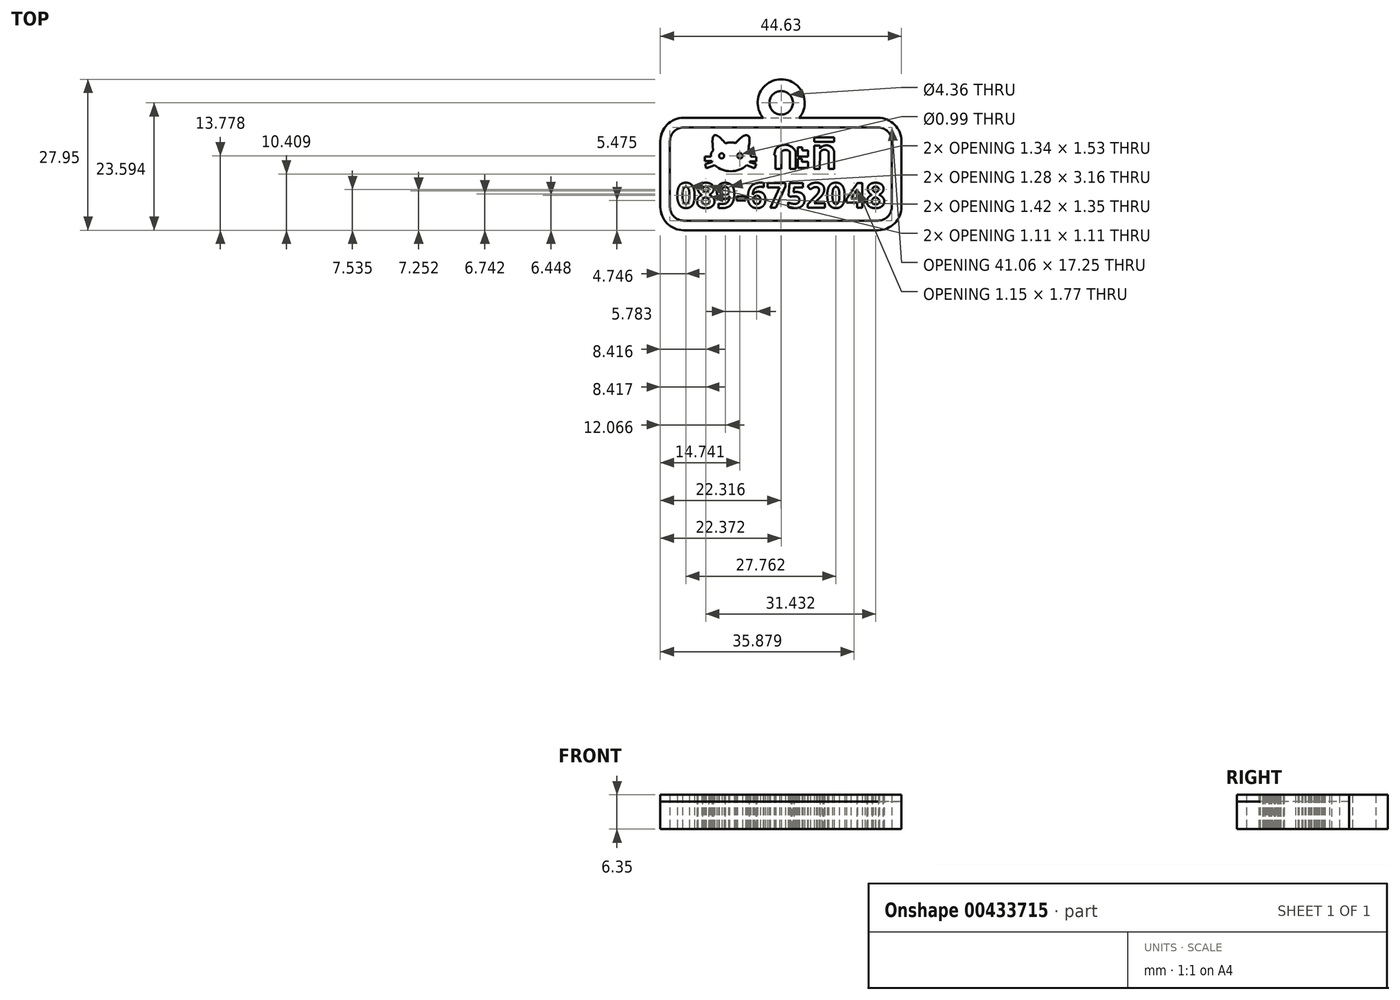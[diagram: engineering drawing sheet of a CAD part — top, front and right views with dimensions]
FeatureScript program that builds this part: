
annotation { "Feature Type Name" : "Feature", "Feature Type Description" : "" }
export const myFeature = defineFeature(function(context is Context, id is Id, definition is map)
    precondition{}
    {
        {
            var Q0;
            Q0=qCreatedBy(makeId("Top.planeOp"),FACE);
            var sketch = newSketch(context, id + "F0", { "sketchPlane" : qUnion([Q0])});
            skPoint(sketch, "E0.middle", {"position": v(0, 0) * mm});
            skLineSegment(sketch, "E1", {"start": v(-2.05, 4.59) * mm, "end": v(-3.13, 4.59) * mm});
            skLineSegment(sketch, "E2", {"start": v(-3.13, 4.59) * mm, "end": v(-3.13, 7.1) * mm});
            skLineSegment(sketch, "E3", {"start": v(-3.13, 7.1) * mm, "end": v(-3.43, 7.1) * mm});
            skLineSegment(sketch, "E4", {"start": v(-3.43, 7.1) * mm, "end": v(-3.16, 8.15) * mm});
            skLineSegment(sketch, "E5", {"start": v(-2.05, 6.13) * mm, "end": v(-2.05, 7.74) * mm});
            skLineSegment(sketch, "E6", {"start": v(-0.46, 7.74) * mm, "end": v(-0.46, 4.59) * mm});
            skLineSegment(sketch, "E7", {"start": v(-0.46, 4.59) * mm, "end": v(0.6, 4.59) * mm});
            skLineSegment(sketch, "E8", {"start": v(0.6, 4.59) * mm, "end": v(0.6, 7.74) * mm});
            skArc(sketch, "E9", {"start": v(-0.46, 7.74) * mm, "mid": v(-1.25, 8.09) * mm, "end": v(-2.05, 7.74) * mm});
            skArc(sketch, "E10", {"start": v(0.6, 7.74) * mm, "mid": v(-1.16, 9.03) * mm, "end": v(-3.16, 8.15) * mm});
            skLineSegment(sketch, "E11", {"start": v(4, 8.88) * mm, "end": v(4, 4.6) * mm});
            skLineSegment(sketch, "E12", {"start": v(4, 4.6) * mm, "end": v(5.01, 4.57) * mm});
            skLineSegment(sketch, "E13", {"start": v(5.01, 4.57) * mm, "end": v(5.08, 7.6) * mm});
            skLineSegment(sketch, "E14", {"start": v(4, 8.88) * mm, "end": v(5.08, 8.88) * mm});
            skLineSegment(sketch, "E15", {"start": v(5.08, 8.88) * mm, "end": v(5.08, 8.34) * mm});
            skLineSegment(sketch, "E16", {"start": v(6.67, 7.73) * mm, "end": v(6.67, 4.57) * mm});
            skLineSegment(sketch, "E17", {"start": v(6.67, 4.57) * mm, "end": v(7.69, 4.57) * mm});
            skLineSegment(sketch, "E18", {"start": v(7.69, 4.57) * mm, "end": v(7.69, 7.91) * mm});
            skArc(sketch, "E19", {"start": v(6.67, 7.73) * mm, "mid": v(5.83, 8.14) * mm, "end": v(5.08, 7.6) * mm});
            skArc(sketch, "E20", {"start": v(7.69, 7.91) * mm, "mid": v(6.51, 8.92) * mm, "end": v(5.08, 8.34) * mm});
            skArc(sketch, "E21", {"start": v(-14.39, 5.28) * mm, "mid": v(-11.44, 4.14) * mm, "end": v(-8.47, 5.26) * mm});
            skArc(sketch, "E22", {"start": v(-14.68, 7.95) * mm, "mid": v(-15.06, 7.46) * mm, "end": v(-15.09, 6.84) * mm});
            skArc(sketch, "E23", {"start": v(-7.74, 6.82) * mm, "mid": v(-7.8, 7.5) * mm, "end": v(-8.2, 8.06) * mm});
            skArc(sketch, "E24", {"start": v(-10.53, 9.35) * mm, "mid": v(-11.47, 9.48) * mm, "end": v(-12.4, 9.32) * mm});
            skFitSpline(sketch, "E25", {"points": [v(-14.68, 7.95) * mm, v(-14.68, 10.54) * mm, v(-14.14, 10.82) * mm, v(-12.4, 9.32) * mm], "startDerivative": vector(-0.83, 7.67) * mm, "endDerivative": vector(4.95, -5.37) * mm});
            skFitSpline(sketch, "E26", {"points": [v(-10.53, 9.35) * mm, v(-8.8, 10.8) * mm, v(-8.08, 10.55) * mm, v(-8.2, 8.06) * mm], "startDerivative": vector(4.76, 5.13) * mm, "endDerivative": vector(-1.39, -7.64) * mm});
            skLineSegment(sketch, "E27", {"start": v(-15.09, 6.84) * mm, "end": v(-16.26, 6.84) * mm});
            skLineSegment(sketch, "E28", {"start": v(-16.26, 6.84) * mm, "end": v(-16.26, 6.04) * mm});
            skLineSegment(sketch, "E29", {"start": v(-16.26, 6.04) * mm, "end": v(-14.93, 6.04) * mm});
            skLineSegment(sketch, "E30", {"start": v(-14.93, 6.04) * mm, "end": v(-14.84, 5.83) * mm});
            skLineSegment(sketch, "E31", {"start": v(-14.84, 5.83) * mm, "end": v(-16.2, 5.45) * mm});
            skLineSegment(sketch, "E32", {"start": v(-16.2, 5.45) * mm, "end": v(-15.98, 4.69) * mm});
            skLineSegment(sketch, "E33", {"start": v(-15.98, 4.69) * mm, "end": v(-14.39, 5.28) * mm});
            skLineSegment(sketch, "E34", {"start": v(-8.47, 5.26) * mm, "end": v(-7.05, 4.67) * mm});
            skLineSegment(sketch, "E35", {"start": v(-7.05, 4.67) * mm, "end": v(-6.74, 5.44) * mm});
            skLineSegment(sketch, "E36", {"start": v(-6.74, 5.44) * mm, "end": v(-7.97, 5.83) * mm});
            skLineSegment(sketch, "E37", {"start": v(-7.97, 5.83) * mm, "end": v(-7.92, 5.99) * mm});
            skLineSegment(sketch, "E38", {"start": v(-7.92, 5.99) * mm, "end": v(-6.68, 5.99) * mm});
            skLineSegment(sketch, "E39", {"start": v(-6.68, 5.99) * mm, "end": v(-6.68, 6.78) * mm});
            skLineSegment(sketch, "E40", {"start": v(-6.68, 6.78) * mm, "end": v(-7.74, 6.82) * mm});
            skCircle(sketch, "E41", {"center": v(-13.12, 6.99) * mm, "radius": 0.47 * mm});
            skCircle(sketch, "E42", {"center": v(-9.73, 7) * mm, "radius": 0.5 * mm});
            skText(sketch, "E43", { "text": "089-6752048", "fontName": "OpenSans-Bold.ttf"});
            skPoint(sketch, "E44.visualSharp", {"position": v(-24.9, 13.73) * mm});
            skPoint(sketch, "E45.visualSharp", {"position": v(21.18, 13.73) * mm});
            skPoint(sketch, "E46.visualSharp", {"position": v(21.18, -6.95) * mm});
            skPoint(sketch, "E47.visualSharp", {"position": v(-24.9, -6.95) * mm});
            skLineSegment(sketch, "E48", {"start": v(-2.05, 6.13) * mm, "end": v(-2.05, 4.59) * mm});
            skPoint(sketch, "E49.orphan", {"position": v(-1.47, 4.59) * mm});
            skLineSegment(sketch, "E50", {"start": v(0.98, 8) * mm, "end": v(0.98, 6.87) * mm});
            skLineSegment(sketch, "E51", {"start": v(0.98, 6.87) * mm, "end": v(2.86, 6.87) * mm});
            skLineSegment(sketch, "E52", {"start": v(2.86, 6.87) * mm, "end": v(2.86, 8) * mm});
            skLineSegment(sketch, "E53", {"start": v(2.86, 8) * mm, "end": v(1.77, 8) * mm});
            skLineSegment(sketch, "E54", {"start": v(1.77, 8) * mm, "end": v(1.77, 8.54) * mm});
            skLineSegment(sketch, "E55", {"start": v(1.77, 8.54) * mm, "end": v(0.98, 8.54) * mm});
            skLineSegment(sketch, "E56", {"start": v(0.98, 8.54) * mm, "end": v(0.98, 8) * mm});
            skLineSegment(sketch, "E57", {"start": v(0.98, 5.9) * mm, "end": v(0.98, 4.77) * mm});
            skLineSegment(sketch, "E58", {"start": v(0.98, 4.77) * mm, "end": v(2.85, 4.77) * mm});
            skLineSegment(sketch, "E59", {"start": v(2.85, 4.77) * mm, "end": v(2.85, 5.9) * mm});
            skLineSegment(sketch, "E60", {"start": v(2.85, 5.9) * mm, "end": v(1.76, 5.9) * mm});
            skLineSegment(sketch, "E61", {"start": v(1.76, 5.9) * mm, "end": v(1.76, 6.44) * mm});
            skLineSegment(sketch, "E62", {"start": v(1.76, 6.44) * mm, "end": v(0.98, 6.44) * mm});
            skLineSegment(sketch, "E63", {"start": v(0.98, 6.44) * mm, "end": v(0.98, 5.89) * mm});
            skLineSegment(sketch, "E64.bottom", {"start": v(4, 9.59) * mm, "end": v(7.69, 9.59) * mm});
            skLineSegment(sketch, "E64.top", {"start": v(4, 10.4) * mm, "end": v(7.69, 10.4) * mm});
            skLineSegment(sketch, "E64.left", {"start": v(4, 9.59) * mm, "end": v(4, 10.4) * mm});
            skLineSegment(sketch, "E64.right", {"start": v(7.69, 9.59) * mm, "end": v(7.69, 10.4) * mm});
            const initialGuessF0  = {"E43": [-0.02156, -0.00263, 1, 0, 0.00463]};
            skSetInitialGuess(sketch, initialGuessF0);
            skSolve(sketch);
        }
        {
            var Q0;
            Q0 = qSketchRegion(id + "F0", true);
            extrude(context, id + "F1", {"entities" : qUnion([Q0]), "depth" : 6.35 * mm});
        }
        {
            var Q0;
            Q0=qCreatedBy(makeId("Top.planeOp"),FACE);
            var sketch = newSketch(context, id + "F2", { "sketchPlane" : qUnion([Q0])});
            skLineSegment(sketch, "E65.bottom", {"start": v(-20.15, 12.25) * mm, "end": v(15.84, 12.25) * mm});
            skLineSegment(sketch, "E65.top", {"start": v(-20.15, -5) * mm, "end": v(15.84, -5) * mm});
            skLineSegment(sketch, "E65.left", {"start": v(-22.69, 9.71) * mm, "end": v(-22.69, -2.46) * mm});
            skLineSegment(sketch, "E65.right", {"start": v(18.38, 9.71) * mm, "end": v(18.38, -2.46) * mm});
            skArc(sketch, "E66.filletArc", {"start": v(-20.15, 12.25) * mm, "mid": v(-21.94, 11.51) * mm, "end": v(-22.69, 9.71) * mm});
            skArc(sketch, "E67.filletArc", {"start": v(18.38, 9.71) * mm, "mid": v(17.63, 11.51) * mm, "end": v(15.84, 12.25) * mm});
            skArc(sketch, "E68.filletArc", {"start": v(15.84, -5) * mm, "mid": v(17.63, -4.25) * mm, "end": v(18.38, -2.46) * mm});
            skArc(sketch, "E69.filletArc", {"start": v(-22.69, -2.46) * mm, "mid": v(-21.94, -4.25) * mm, "end": v(-20.15, -5) * mm});
            skArc(sketch, "E70.0", {"start": v(-20.15, 14.03) * mm, "mid": v(-23.2, 12.77) * mm, "end": v(-24.46, 9.71) * mm});
            skLineSegment(sketch, "E70.1", {"start": v(-24.46, 9.71) * mm, "end": v(-24.46, -2.46) * mm});
            skLineSegment(sketch, "E70.2", {"start": v(-20.15, 14.03) * mm, "end": v(15.84, 14.03) * mm});
            skArc(sketch, "E70.3", {"start": v(-24.46, -2.46) * mm, "mid": v(-23.2, -5.51) * mm, "end": v(-20.15, -6.78) * mm});
            skArc(sketch, "E70.4", {"start": v(20.16, 9.71) * mm, "mid": v(18.9, 12.77) * mm, "end": v(15.84, 14.03) * mm});
            skLineSegment(sketch, "E70.5", {"start": v(20.16, 9.71) * mm, "end": v(20.16, -2.46) * mm});
            skArc(sketch, "E70.6", {"start": v(15.84, -6.78) * mm, "mid": v(18.9, -5.51) * mm, "end": v(20.16, -2.46) * mm});
            skLineSegment(sketch, "E70.7", {"start": v(-20.15, -6.78) * mm, "end": v(15.84, -6.78) * mm});
            skCircle(sketch, "E71", {"center": v(-2.1, 16.81) * mm, "radius": 4.36 * mm});
            skCircle(sketch, "E72", {"center": v(-2.1, 16.81) * mm, "radius": 2.18 * mm});
            skSolve(sketch);
        }
        {
            var Q0;
            Q0 = qSketchRegion(id + "F2", true);
            extrude(context, id + "F3", {"entities" : qUnion([Q0]), "depth" : 6.35 * mm});
        }
        {
            var Q0;
            Q0=qCreatedBy(makeId("Top.planeOp"),FACE);
            var sketch = newSketch(context, id + "F4", { "sketchPlane" : qUnion([Q0])});
            skArc(sketch, "E73.0", {"start": v(-20.15, 14.03) * mm, "mid": v(-23.2, 12.77) * mm, "end": v(-24.47, 9.71) * mm});
            skLineSegment(sketch, "E73.1", {"start": v(-24.47, 9.71) * mm, "end": v(-24.47, -2.46) * mm});
            skLineSegment(sketch, "E73.2", {"start": v(-20.15, 14.03) * mm, "end": v(15.83, 14.03) * mm});
            skArc(sketch, "E73.3", {"start": v(-24.47, -2.46) * mm, "mid": v(-23.2, -5.51) * mm, "end": v(-20.15, -6.78) * mm});
            skArc(sketch, "E73.4", {"start": v(20.15, 9.71) * mm, "mid": v(18.89, 12.77) * mm, "end": v(15.83, 14.03) * mm});
            skLineSegment(sketch, "E73.5", {"start": v(20.15, 9.71) * mm, "end": v(20.15, -2.46) * mm});
            skArc(sketch, "E73.6", {"start": v(15.83, -6.78) * mm, "mid": v(18.89, -5.51) * mm, "end": v(20.15, -2.46) * mm});
            skLineSegment(sketch, "E73.7", {"start": v(-20.15, -6.78) * mm, "end": v(15.83, -6.78) * mm});
            skSolve(sketch);
        }
        {
            var Q0;
            Q0 = qSketchRegion(id + "F4", true);
            extrude(context, id + "F5", {"entities" : qUnion([Q0]), "depth" : 5.08 * mm});
        }
    });
